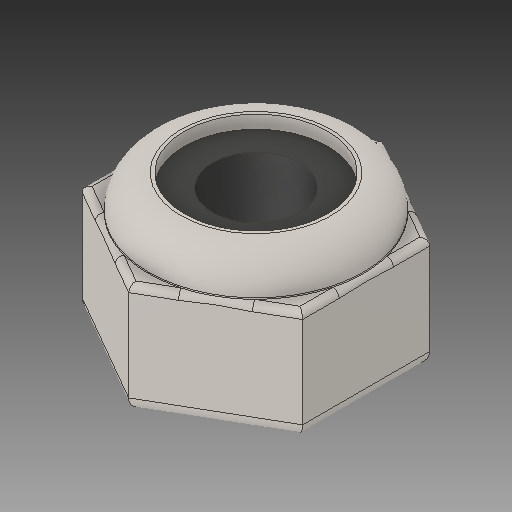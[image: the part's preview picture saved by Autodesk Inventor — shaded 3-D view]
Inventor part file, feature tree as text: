
AUTODESK INVENTOR PART (.ipt)
format: ipt  version: 2018 (Build 220112000, 112)  size: 202,752 bytes
history: native  units: in
note: dims shown in document units (in); Inventor stores cm internally (conversion verified against a paired STEP export)
features: fillet x1
ambient origin geometry x8: Origin, YZ Plane, XZ Plane, XY Plane, X Axis, Y Axis, Z Axis, Center Point
bodies: Solid1 (feature_tree)
feature tree (1):
  fillet  "Fillet6"  [1 undecoded]
note: 1 required parameter value undecoded (feature->parameter linkage not recoverable at this tier; creation-order binding heuristic only, values carry confidence <= 0.55)
